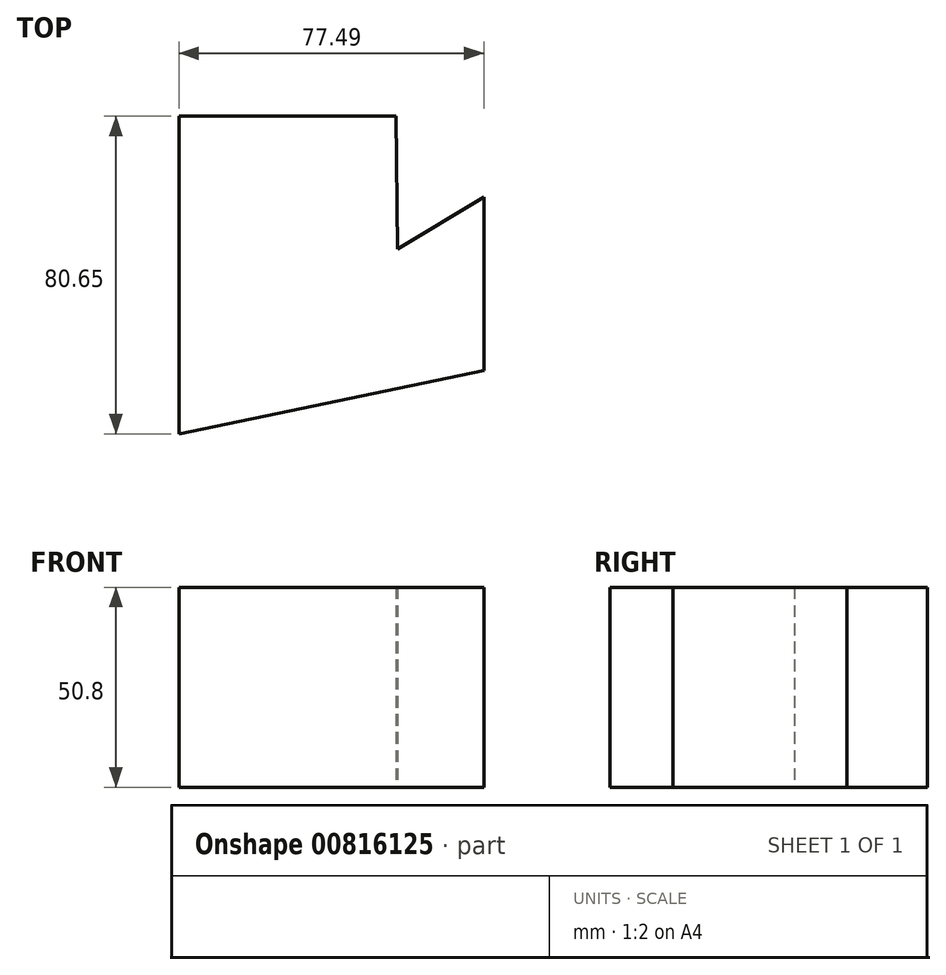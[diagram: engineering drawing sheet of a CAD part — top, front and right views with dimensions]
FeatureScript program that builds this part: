
annotation { "Feature Type Name" : "Feature", "Feature Type Description" : "" }
export const myFeature = defineFeature(function(context is Context, id is Id, definition is map)
    precondition{}
    {
        {
            var Q0;
            Q0=qCreatedBy(makeId("Top.planeOp"),FACE);
            var sketch = newSketch(context, id + "F0", { "sketchPlane" : qUnion([Q0])});
            skLineSegment(sketch, "E0", {"start": v(-28.12, -34.06) * mm, "end": v(-28.12, 46.6) * mm});
            skLineSegment(sketch, "E1", {"start": v(-28.12, 46.6) * mm, "end": v(26.99, 46.6) * mm});
            skLineSegment(sketch, "E2", {"start": v(26.99, 46.6) * mm, "end": v(27.4, 12.81) * mm});
            skLineSegment(sketch, "E3", {"start": v(27.4, 12.81) * mm, "end": v(49.37, 26.11) * mm});
            skLineSegment(sketch, "E4", {"start": v(49.37, 26.11) * mm, "end": v(49.37, -18.01) * mm});
            skLineSegment(sketch, "E5", {"start": v(49.37, -18.01) * mm, "end": v(-28.12, -34.06) * mm});
            skSolve(sketch);
        }
        {
            var Q0;
            Q0 = qSketchRegion(id + "F0", true);
            extrude(context, id + "F1", {"entities" : qUnion([Q0]), "depth" : 50.8 * mm, "offsetDistance" : 25.4 * mm});
        }
    });
